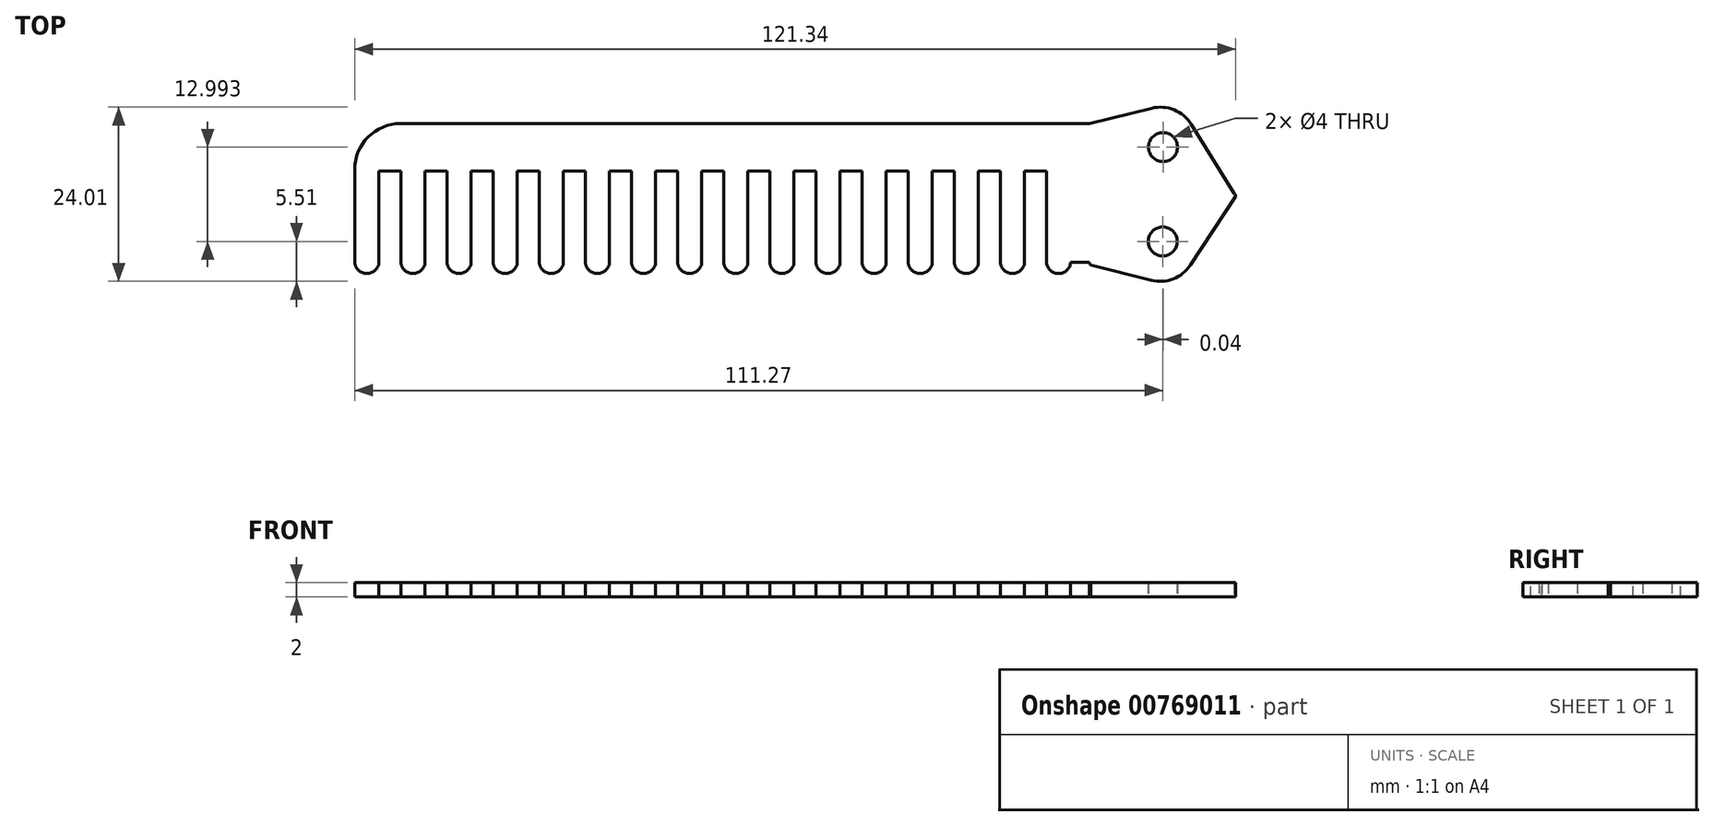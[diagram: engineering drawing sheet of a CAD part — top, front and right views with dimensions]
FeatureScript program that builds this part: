
annotation { "Feature Type Name" : "Feature", "Feature Type Description" : "" }
export const myFeature = defineFeature(function(context is Context, id is Id, definition is map)
    precondition{}
    {
        {
            var Q0;
            Q0=qCreatedBy(makeId("Top.planeOp"),FACE);
            var sketch = newSketch(context, id + "F0", { "sketchPlane" : qUnion([Q0])});
            skLineSegment(sketch, "E0", {"start": v(-47.53, 12.92) * mm, "end": v(-47.53, 1.96) * mm});
            skArc(sketch, "E1.filletArc", {"start": v(-44.5, 15.95) * mm, "mid": v(-46.64, 15.07) * mm, "end": v(-47.53, 12.92) * mm});
            skArc(sketch, "E2.filletArc", {"start": v(58.65, -3.18) * mm, "mid": v(58.7, -3.38) * mm, "end": v(58.81, -3.55) * mm});
            skLineSegment(sketch, "E3", {"start": v(78.8, 5.95) * mm, "end": v(78.8, 5.95) * mm});
            skLineSegment(sketch, "E4", {"start": v(-44.5, 15.95) * mm, "end": v(58.65, 15.95) * mm});
            skPoint(sketch, "E5.visualSharp", {"position": v(78.8, -4.05) * mm});
            skPoint(sketch, "E6.visualSharp", {"position": v(78.8, 15.95) * mm});
            skPoint(sketch, "E7.visualSharp", {"position": v(78.8, 5.95) * mm});
            skCircle(sketch, "E8", {"center": v(68.73, -0.29) * mm, "radius": 2 * mm});
            skCircle(sketch, "E9", {"center": v(68.77, 12.7) * mm, "radius": 2 * mm});
            skLineSegment(sketch, "E10", {"start": v(72.54, -3.55) * mm, "end": v(78.8, 5.94) * mm});
            skLineSegment(sketch, "E11", {"start": v(72.66, 15.85) * mm, "end": v(78.6, 6.3) * mm});
            skLineSegment(sketch, "E12", {"start": v(58.65, 15.95) * mm, "end": v(67.22, 18.06) * mm});
            skLineSegment(sketch, "E13", {"start": v(58.81, -3.55) * mm, "end": v(67.14, -5.65) * mm});
            skPoint(sketch, "E14.visualSharp", {"position": v(70.75, 18.93) * mm});
            skArc(sketch, "E14.filletArc", {"start": v(72.66, 15.85) * mm, "mid": v(70.3, 17.84) * mm, "end": v(67.22, 18.06) * mm});
            skPoint(sketch, "E15.visualSharp", {"position": v(70.58, -6.52) * mm});
            skArc(sketch, "E15.filletArc", {"start": v(67.14, -5.65) * mm, "mid": v(70.17, -5.46) * mm, "end": v(72.54, -3.55) * mm});
            skArc(sketch, "E16", {"start": v(78.8, 5.94) * mm, "mid": v(78.72, 6.13) * mm, "end": v(78.6, 6.3) * mm});
            skLineSegment(sketch, "E17", {"start": v(-42.54, -3.04) * mm, "end": v(58.65, -3.18) * mm});
            skPoint(sketch, "E18.visualSharp", {"position": v(-47.53, -3.03) * mm});
            skArc(sketch, "E18.filletArc", {"start": v(-47.53, 1.96) * mm, "mid": v(-46.07, -1.57) * mm, "end": v(-42.54, -3.04) * mm});
            skSolve(sketch);
        }
        {
            var Q0;
            Q0=qSketchRegion(id+"F0",true);
            var Q1;
            Q1=makeQuery(id+"F0.imprint","IMPRINT",FACE,{"disambiguationData":[TD([[makeQuery(id+"F0.imprint","IMPRINT",EDGE,{"derivedFrom":sQuery(id+"F0.wireOp",EDGE,"1oXmgVZ5-gnLq-iHea-oESG-ihjMs6EF8sqd")}),1.0]])]});
            var Q2;
            Q2=makeQuery(id+"F0.imprint","IMPRINT",FACE,{"disambiguationData":[TD([[makeQuery(id+"F0.imprint","IMPRINT",EDGE,{"derivedFrom":sQuery(id+"F0.wireOp",EDGE,"hkDLLBfR-qxi3-HcG5-FM2N-qt6i9bJRYM3o")}),1.0]])]});
            extrude(context, id + "F1", {"entities" : qUnion([Q0, Q1, Q2]), "depth" : 2 * mm, "offsetDistance" : 25 * mm});
        }
        {
            var Q0;
            Q0=makeQuery(id+"F1.opExtrude","CAP_FACE",FACE,{"disambiguationData":[OSD([sQuery(id+"F0.wireOp",EDGE,"E0"),sQuery(id+"F0.wireOp",EDGE,"E1.filletArc"),sQuery(id+"F0.wireOp",EDGE,"E2.filletArc"),sQuery(id+"F0.wireOp",EDGE,"E4"),sQuery(id+"F0.wireOp",EDGE,"E8"),sQuery(id+"F0.wireOp",EDGE,"E9"),sQuery(id+"F0.wireOp",EDGE,"E10"),sQuery(id+"F0.wireOp",EDGE,"E11"),sQuery(id+"F0.wireOp",EDGE,"E12"),sQuery(id+"F0.wireOp",EDGE,"E13"),sQuery(id+"F0.wireOp",EDGE,"E14.filletArc"),sQuery(id+"F0.wireOp",EDGE,"E15.filletArc"),sQuery(id+"F0.wireOp",EDGE,"E16"),sQuery(id+"F0.wireOp",EDGE,"E17"),sQuery(id+"F0.wireOp",EDGE,"E18.filletArc")])],"isStart":false});
            var sketch = newSketch(context, id + "F2", { "sketchPlane" : qUnion([Q0])});
            skLineSegment(sketch, "E19.0", {"start": v(-36.19, 15.95) * mm, "end": v(58.65, 15.95) * mm});
            skLineSegment(sketch, "E20", {"start": v(-42.54, -3.04) * mm, "end": v(-42.54, 9.41) * mm});
            skLineSegment(sketch, "E21", {"start": v(-42.54, 9.41) * mm, "end": v(-39.18, 9.41) * mm});
            skLineSegment(sketch, "E22", {"start": v(-39.18, 9.41) * mm, "end": v(-39.18, -3.05) * mm});
            skArc(sketch, "E23", {"start": v(-42.54, -3.04) * mm, "mid": v(-40.86, -4.72) * mm, "end": v(-39.18, -3.05) * mm});
            skArc(sketch, "E24.1.0.0", {"start": v(-36.19, -3.04) * mm, "mid": v(-34.51, -4.72) * mm, "end": v(-32.83, -3.05) * mm});
            skLineSegment(sketch, "E24.1.0.1", {"start": v(-32.83, 9.41) * mm, "end": v(-32.83, -3.05) * mm});
            skLineSegment(sketch, "E24.1.0.2", {"start": v(-36.19, 9.41) * mm, "end": v(-32.83, 9.41) * mm});
            skLineSegment(sketch, "E24.1.0.3", {"start": v(-36.19, -3.04) * mm, "end": v(-36.19, 9.41) * mm});
            skArc(sketch, "E24.2.0.0", {"start": v(-29.84, -3.04) * mm, "mid": v(-28.16, -4.72) * mm, "end": v(-26.48, -3.05) * mm});
            skLineSegment(sketch, "E24.2.0.1", {"start": v(-26.48, 9.41) * mm, "end": v(-26.48, -3.05) * mm});
            skLineSegment(sketch, "E24.2.0.2", {"start": v(-29.84, 9.41) * mm, "end": v(-26.48, 9.41) * mm});
            skLineSegment(sketch, "E24.2.0.3", {"start": v(-29.84, -3.04) * mm, "end": v(-29.84, 9.41) * mm});
            skArc(sketch, "E24.3.0.0", {"start": v(-23.49, -3.04) * mm, "mid": v(-21.81, -4.72) * mm, "end": v(-20.13, -3.05) * mm});
            skLineSegment(sketch, "E24.3.0.1", {"start": v(-20.13, 9.41) * mm, "end": v(-20.13, -3.05) * mm});
            skLineSegment(sketch, "E24.3.0.2", {"start": v(-23.49, 9.41) * mm, "end": v(-20.13, 9.41) * mm});
            skLineSegment(sketch, "E24.3.0.3", {"start": v(-23.49, -3.04) * mm, "end": v(-23.49, 9.41) * mm});
            skArc(sketch, "E24.4.0.0", {"start": v(-17.14, -3.04) * mm, "mid": v(-15.46, -4.72) * mm, "end": v(-13.78, -3.05) * mm});
            skLineSegment(sketch, "E24.4.0.1", {"start": v(-13.78, 9.41) * mm, "end": v(-13.78, -3.05) * mm});
            skLineSegment(sketch, "E24.4.0.2", {"start": v(-17.14, 9.41) * mm, "end": v(-13.78, 9.41) * mm});
            skLineSegment(sketch, "E24.4.0.3", {"start": v(-17.14, -3.04) * mm, "end": v(-17.14, 9.41) * mm});
            skArc(sketch, "E24.5.0.0", {"start": v(-10.79, -3.04) * mm, "mid": v(-9.11, -4.72) * mm, "end": v(-7.43, -3.05) * mm});
            skLineSegment(sketch, "E24.5.0.1", {"start": v(-7.43, 9.41) * mm, "end": v(-7.43, -3.05) * mm});
            skLineSegment(sketch, "E24.5.0.2", {"start": v(-10.79, 9.41) * mm, "end": v(-7.43, 9.41) * mm});
            skLineSegment(sketch, "E24.5.0.3", {"start": v(-10.79, -3.04) * mm, "end": v(-10.79, 9.41) * mm});
            skArc(sketch, "E24.6.0.0", {"start": v(-4.44, -3.04) * mm, "mid": v(-2.76, -4.72) * mm, "end": v(-1.08, -3.05) * mm});
            skLineSegment(sketch, "E24.6.0.1", {"start": v(-1.08, 9.41) * mm, "end": v(-1.08, -3.05) * mm});
            skLineSegment(sketch, "E24.6.0.2", {"start": v(-4.44, 9.41) * mm, "end": v(-1.08, 9.41) * mm});
            skLineSegment(sketch, "E24.6.0.3", {"start": v(-4.44, -3.04) * mm, "end": v(-4.44, 9.41) * mm});
            skArc(sketch, "E24.7.0.0", {"start": v(1.91, -3.04) * mm, "mid": v(3.59, -4.72) * mm, "end": v(5.27, -3.05) * mm});
            skLineSegment(sketch, "E24.7.0.1", {"start": v(5.27, 9.41) * mm, "end": v(5.27, -3.05) * mm});
            skLineSegment(sketch, "E24.7.0.2", {"start": v(1.91, 9.41) * mm, "end": v(5.27, 9.41) * mm});
            skLineSegment(sketch, "E24.7.0.3", {"start": v(1.91, -3.04) * mm, "end": v(1.91, 9.41) * mm});
            skArc(sketch, "E24.8.0.0", {"start": v(8.26, -3.04) * mm, "mid": v(9.94, -4.72) * mm, "end": v(11.62, -3.05) * mm});
            skLineSegment(sketch, "E24.8.0.1", {"start": v(11.62, 9.41) * mm, "end": v(11.62, -3.05) * mm});
            skLineSegment(sketch, "E24.8.0.2", {"start": v(8.26, 9.41) * mm, "end": v(11.62, 9.41) * mm});
            skLineSegment(sketch, "E24.8.0.3", {"start": v(8.26, -3.04) * mm, "end": v(8.26, 9.41) * mm});
            skLineSegment(sketch, "E25.1.0.0", {"start": v(17.97, 9.41) * mm, "end": v(17.97, -3.05) * mm});
            skLineSegment(sketch, "E25.1.0.1", {"start": v(14.61, -3.04) * mm, "end": v(14.61, 9.41) * mm});
            skArc(sketch, "E25.1.0.2", {"start": v(14.61, -3.04) * mm, "mid": v(16.29, -4.72) * mm, "end": v(17.97, -3.05) * mm});
            skLineSegment(sketch, "E25.1.0.3", {"start": v(14.61, 9.41) * mm, "end": v(17.97, 9.41) * mm});
            skLineSegment(sketch, "E25.2.0.0", {"start": v(24.32, 9.41) * mm, "end": v(24.32, -3.05) * mm});
            skLineSegment(sketch, "E25.2.0.1", {"start": v(20.96, -3.04) * mm, "end": v(20.96, 9.41) * mm});
            skArc(sketch, "E25.2.0.2", {"start": v(20.96, -3.04) * mm, "mid": v(22.64, -4.72) * mm, "end": v(24.32, -3.05) * mm});
            skLineSegment(sketch, "E25.2.0.3", {"start": v(20.96, 9.41) * mm, "end": v(24.32, 9.41) * mm});
            skLineSegment(sketch, "E25.3.0.0", {"start": v(30.67, 9.41) * mm, "end": v(30.67, -3.05) * mm});
            skLineSegment(sketch, "E25.3.0.1", {"start": v(27.31, -3.04) * mm, "end": v(27.31, 9.41) * mm});
            skArc(sketch, "E25.3.0.2", {"start": v(27.31, -3.04) * mm, "mid": v(28.99, -4.72) * mm, "end": v(30.67, -3.05) * mm});
            skLineSegment(sketch, "E25.3.0.3", {"start": v(27.31, 9.41) * mm, "end": v(30.67, 9.41) * mm});
            skLineSegment(sketch, "E25.4.0.0", {"start": v(37.02, 9.41) * mm, "end": v(37.02, -3.05) * mm});
            skLineSegment(sketch, "E25.4.0.1", {"start": v(33.66, -3.04) * mm, "end": v(33.66, 9.41) * mm});
            skArc(sketch, "E25.4.0.2", {"start": v(33.66, -3.04) * mm, "mid": v(35.34, -4.72) * mm, "end": v(37.02, -3.05) * mm});
            skLineSegment(sketch, "E25.4.0.3", {"start": v(33.66, 9.41) * mm, "end": v(37.02, 9.41) * mm});
            skLineSegment(sketch, "E25.5.0.0", {"start": v(43.37, 9.41) * mm, "end": v(43.37, -3.05) * mm});
            skLineSegment(sketch, "E25.5.0.1", {"start": v(40.01, -3.04) * mm, "end": v(40.01, 9.41) * mm});
            skArc(sketch, "E25.5.0.2", {"start": v(40.01, -3.04) * mm, "mid": v(41.69, -4.72) * mm, "end": v(43.37, -3.05) * mm});
            skLineSegment(sketch, "E25.5.0.3", {"start": v(40.01, 9.41) * mm, "end": v(43.37, 9.41) * mm});
            skLineSegment(sketch, "E25.6.0.0", {"start": v(49.72, 9.41) * mm, "end": v(49.72, -3.05) * mm});
            skLineSegment(sketch, "E25.6.0.1", {"start": v(46.36, -3.04) * mm, "end": v(46.36, 9.41) * mm});
            skArc(sketch, "E25.6.0.2", {"start": v(46.36, -3.04) * mm, "mid": v(48.04, -4.72) * mm, "end": v(49.72, -3.05) * mm});
            skLineSegment(sketch, "E25.6.0.3", {"start": v(46.36, 9.41) * mm, "end": v(49.72, 9.41) * mm});
            skLineSegment(sketch, "E25.7.0.0", {"start": v(56.07, 9.41) * mm, "end": v(56.07, -3.05) * mm});
            skLineSegment(sketch, "E25.7.0.1", {"start": v(52.71, -3.04) * mm, "end": v(52.71, 9.41) * mm});
            skArc(sketch, "E25.7.0.2", {"start": v(52.71, -3.04) * mm, "mid": v(54.39, -4.72) * mm, "end": v(56.07, -3.05) * mm});
            skLineSegment(sketch, "E25.7.0.3", {"start": v(52.71, 9.41) * mm, "end": v(56.07, 9.41) * mm});
            skLineSegment(sketch, "E25.direction1", {"start": v(8.26, -3.04) * mm, "end": v(14.61, -3.04) * mm, "construction": true});
            skLineSegment(sketch, "E26", {"start": v(-39.18, 9.41) * mm, "end": v(-36.19, 9.41) * mm});
            skLineSegment(sketch, "E27", {"start": v(-32.83, 9.41) * mm, "end": v(-29.84, 9.41) * mm});
            skLineSegment(sketch, "E28", {"start": v(-26.48, 9.41) * mm, "end": v(-23.49, 9.41) * mm});
            skLineSegment(sketch, "E29", {"start": v(-20.13, 9.41) * mm, "end": v(-17.14, 9.41) * mm});
            skLineSegment(sketch, "E30", {"start": v(-13.78, 9.41) * mm, "end": v(-10.79, 9.41) * mm});
            skLineSegment(sketch, "E31", {"start": v(-7.43, 9.41) * mm, "end": v(-4.44, 9.41) * mm});
            skLineSegment(sketch, "E32", {"start": v(-1.08, 9.41) * mm, "end": v(1.91, 9.41) * mm});
            skLineSegment(sketch, "E33", {"start": v(5.27, 9.41) * mm, "end": v(8.26, 9.41) * mm});
            skLineSegment(sketch, "E34", {"start": v(11.62, 9.41) * mm, "end": v(14.61, 9.41) * mm});
            skLineSegment(sketch, "E35", {"start": v(17.97, 9.41) * mm, "end": v(20.96, 9.41) * mm});
            skLineSegment(sketch, "E36", {"start": v(24.32, 9.41) * mm, "end": v(27.31, 9.41) * mm});
            skLineSegment(sketch, "E37", {"start": v(30.67, 9.41) * mm, "end": v(33.66, 9.41) * mm});
            skLineSegment(sketch, "E38", {"start": v(37.02, 9.41) * mm, "end": v(40.01, 9.41) * mm});
            skLineSegment(sketch, "E39", {"start": v(43.37, 9.41) * mm, "end": v(46.36, 9.41) * mm});
            skLineSegment(sketch, "E40", {"start": v(49.72, 9.41) * mm, "end": v(52.71, 9.41) * mm});
            skLineSegment(sketch, "E41.0", {"start": v(-42.54, -3.04) * mm, "end": v(58.65, -3.18) * mm});
            skLineSegment(sketch, "E42", {"start": v(-42.54, 9.41) * mm, "end": v(-42.54, 9.6) * mm});
            skPoint(sketch, "E43.orphan", {"position": v(-44.5, 15.95) * mm});
            skPoint(sketch, "E44.visualSharp", {"position": v(-42.54, 15.95) * mm});
            skArc(sketch, "E44.filletArc", {"start": v(-36.19, 15.95) * mm, "mid": v(-40.68, 14.1) * mm, "end": v(-42.54, 9.6) * mm});
            skSolve(sketch);
        }
        {
            var Q0;
            {var subQ4=sQuery(id+"F2.wireOp",EDGE,"E24.4.0.1");Q0=makeQuery(id+"F2.imprint","IMPRINT",FACE,{"disambiguationData":[TD([[makeQuery(id+"F2.imprint","IMPRINT",EDGE,{"derivedFrom":subQ4}),1.0]])]});}
            var Q1;
            {var subQ4=sQuery(id+"F2.wireOp",EDGE,"E24.5.0.1");Q1=makeQuery(id+"F2.imprint","IMPRINT",FACE,{"disambiguationData":[TD([[makeQuery(id+"F2.imprint","IMPRINT",EDGE,{"derivedFrom":subQ4}),1.0]])]});}
            var Q2;
            {var subQ6=sQuery(id+"F2.wireOp",EDGE,"E24.6.0.1");Q2=makeQuery(id+"F2.imprint","IMPRINT",FACE,{"disambiguationData":[TD([[makeQuery(id+"F2.imprint","IMPRINT",EDGE,{"derivedFrom":subQ6}),1.0]])]});}
            var Q3;
            {var subQ4=sQuery(id+"F2.wireOp",EDGE,"E24.7.0.1");Q3=makeQuery(id+"F2.imprint","IMPRINT",FACE,{"disambiguationData":[TD([[makeQuery(id+"F2.imprint","IMPRINT",EDGE,{"derivedFrom":subQ4}),1.0]])]});}
            var Q4;
            {var subQ4=sQuery(id+"F2.wireOp",EDGE,"E24.8.0.1");Q4=makeQuery(id+"F2.imprint","IMPRINT",FACE,{"disambiguationData":[TD([[makeQuery(id+"F2.imprint","IMPRINT",EDGE,{"derivedFrom":subQ4}),1.0]])]});}
            var Q5;
            {var subQ5=sQuery(id+"F2.wireOp",EDGE,"E25.1.0.0");Q5=makeQuery(id+"F2.imprint","IMPRINT",FACE,{"disambiguationData":[TD([[makeQuery(id+"F2.imprint","IMPRINT",EDGE,{"derivedFrom":subQ5}),1.0]])]});}
            var Q6;
            {var subQ5=sQuery(id+"F2.wireOp",EDGE,"E25.2.0.0");Q6=makeQuery(id+"F2.imprint","IMPRINT",FACE,{"disambiguationData":[TD([[makeQuery(id+"F2.imprint","IMPRINT",EDGE,{"derivedFrom":subQ5}),1.0]])]});}
            var Q7;
            {var subQ5=sQuery(id+"F2.wireOp",EDGE,"E25.3.0.0");Q7=makeQuery(id+"F2.imprint","IMPRINT",FACE,{"disambiguationData":[TD([[makeQuery(id+"F2.imprint","IMPRINT",EDGE,{"derivedFrom":subQ5}),1.0]])]});}
            var Q8;
            {var subQ5=sQuery(id+"F2.wireOp",EDGE,"E25.4.0.0");Q8=makeQuery(id+"F2.imprint","IMPRINT",FACE,{"disambiguationData":[TD([[makeQuery(id+"F2.imprint","IMPRINT",EDGE,{"derivedFrom":subQ5}),1.0]])]});}
            var Q9;
            {var subQ5=sQuery(id+"F2.wireOp",EDGE,"E25.5.0.0");Q9=makeQuery(id+"F2.imprint","IMPRINT",FACE,{"disambiguationData":[TD([[makeQuery(id+"F2.imprint","IMPRINT",EDGE,{"derivedFrom":subQ5}),1.0]])]});}
            var Q10;
            {var subQ5=sQuery(id+"F2.wireOp",EDGE,"E25.6.0.0");Q10=makeQuery(id+"F2.imprint","IMPRINT",FACE,{"disambiguationData":[TD([[makeQuery(id+"F2.imprint","IMPRINT",EDGE,{"derivedFrom":subQ5}),1.0]])]});}
            var Q11;
            {var subQ4=sQuery(id+"F2.wireOp",EDGE,"E24.3.0.1");Q11=makeQuery(id+"F2.imprint","IMPRINT",FACE,{"disambiguationData":[TD([[makeQuery(id+"F2.imprint","IMPRINT",EDGE,{"derivedFrom":subQ4}),1.0]])]});}
            var Q12;
            {var subQ4=sQuery(id+"F2.wireOp",EDGE,"E24.2.0.1");Q12=makeQuery(id+"F2.imprint","IMPRINT",FACE,{"disambiguationData":[TD([[makeQuery(id+"F2.imprint","IMPRINT",EDGE,{"derivedFrom":subQ4}),1.0]])]});}
            var Q13;
            {var subQ4=sQuery(id+"F2.wireOp",EDGE,"E24.1.0.1");Q13=makeQuery(id+"F2.imprint","IMPRINT",FACE,{"disambiguationData":[TD([[makeQuery(id+"F2.imprint","IMPRINT",EDGE,{"derivedFrom":subQ4}),1.0]])]});}
            var Q14;
            {var subQ4=sQuery(id+"F2.wireOp",EDGE,"E22");Q14=makeQuery(id+"F2.imprint","IMPRINT",FACE,{"disambiguationData":[TD([[makeQuery(id+"F2.imprint","IMPRINT",EDGE,{"derivedFrom":subQ4}),1.0]])]});}
            extrude(context, id + "F3", {"entities" : qUnion([Q0, Q1, Q2, Q3, Q4, Q5, Q6, Q7, Q8, Q9, Q10, Q11, Q12, Q13, Q14]), "operationType" : NewBodyOperationType.REMOVE, "oppositeDirection" : true, "depth" : 25.4 * mm, "offsetDistance" : 25.4 * mm});
        }
        {
            var Q0;
            {var subQ0=sQuery(id+"F2.wireOp",EDGE,"E41.0");var subQ1=sQuery(id+"F2.wireOp",EDGE,"E25.7.0.2");var subQ2=makeQuery(id+"F2.imprint","INTERSECT",VERTEX,{"disambiguationData":[OD(0.0)],"derivedFrom":[subQ1,subQ0]});Q0=makeQuery(id+"F2.imprint","IMPRINT",FACE,{"disambiguationData":[TD([[makeQuery(id+"F2.imprint","IMPRINT",EDGE,{"disambiguationData":[TD([[subQ2,-1.0]])],"derivedFrom":subQ1}),1.0]])]});}
            var Q1;
            {var subQ0=sQuery(id+"F2.wireOp",EDGE,"E41.0");var subQ1=sQuery(id+"F2.wireOp",EDGE,"E25.6.0.2");var subQ2=makeQuery(id+"F2.imprint","INTERSECT",VERTEX,{"disambiguationData":[OD(0.0)],"derivedFrom":[subQ1,subQ0]});Q1=makeQuery(id+"F2.imprint","IMPRINT",FACE,{"disambiguationData":[TD([[makeQuery(id+"F2.imprint","IMPRINT",EDGE,{"disambiguationData":[TD([[subQ2,-1.0]])],"derivedFrom":subQ1}),1.0]])]});}
            var Q2;
            {var subQ0=sQuery(id+"F2.wireOp",EDGE,"E41.0");var subQ1=sQuery(id+"F2.wireOp",EDGE,"E25.5.0.2");var subQ2=makeQuery(id+"F2.imprint","INTERSECT",VERTEX,{"disambiguationData":[OD(0.0)],"derivedFrom":[subQ1,subQ0]});Q2=makeQuery(id+"F2.imprint","IMPRINT",FACE,{"disambiguationData":[TD([[makeQuery(id+"F2.imprint","IMPRINT",EDGE,{"disambiguationData":[TD([[subQ2,-1.0]])],"derivedFrom":subQ1}),1.0]])]});}
            var Q3;
            {var subQ0=sQuery(id+"F2.wireOp",EDGE,"E41.0");var subQ1=sQuery(id+"F2.wireOp",EDGE,"E25.4.0.2");var subQ2=makeQuery(id+"F2.imprint","INTERSECT",VERTEX,{"disambiguationData":[OD(0.0)],"derivedFrom":[subQ1,subQ0]});Q3=makeQuery(id+"F2.imprint","IMPRINT",FACE,{"disambiguationData":[TD([[makeQuery(id+"F2.imprint","IMPRINT",EDGE,{"disambiguationData":[TD([[subQ2,-1.0]])],"derivedFrom":subQ1}),1.0]])]});}
            var Q4;
            {var subQ0=sQuery(id+"F2.wireOp",EDGE,"E41.0");var subQ1=sQuery(id+"F2.wireOp",EDGE,"E25.3.0.2");var subQ2=makeQuery(id+"F2.imprint","INTERSECT",VERTEX,{"disambiguationData":[OD(0.0)],"derivedFrom":[subQ1,subQ0]});Q4=makeQuery(id+"F2.imprint","IMPRINT",FACE,{"disambiguationData":[TD([[makeQuery(id+"F2.imprint","IMPRINT",EDGE,{"disambiguationData":[TD([[subQ2,-1.0]])],"derivedFrom":subQ1}),1.0]])]});}
            var Q5;
            {var subQ0=sQuery(id+"F2.wireOp",EDGE,"E41.0");var subQ1=sQuery(id+"F2.wireOp",EDGE,"E25.2.0.2");var subQ2=makeQuery(id+"F2.imprint","INTERSECT",VERTEX,{"disambiguationData":[OD(0.0)],"derivedFrom":[subQ1,subQ0]});Q5=makeQuery(id+"F2.imprint","IMPRINT",FACE,{"disambiguationData":[TD([[makeQuery(id+"F2.imprint","IMPRINT",EDGE,{"disambiguationData":[TD([[subQ2,-1.0]])],"derivedFrom":subQ1}),1.0]])]});}
            var Q6;
            {var subQ0=sQuery(id+"F2.wireOp",EDGE,"E41.0");var subQ1=sQuery(id+"F2.wireOp",EDGE,"E25.1.0.2");var subQ2=makeQuery(id+"F2.imprint","INTERSECT",VERTEX,{"disambiguationData":[OD(0.0)],"derivedFrom":[subQ1,subQ0]});Q6=makeQuery(id+"F2.imprint","IMPRINT",FACE,{"disambiguationData":[TD([[makeQuery(id+"F2.imprint","IMPRINT",EDGE,{"disambiguationData":[TD([[subQ2,-1.0]])],"derivedFrom":subQ1}),1.0]])]});}
            var Q7;
            {var subQ0=sQuery(id+"F2.wireOp",EDGE,"E41.0");var subQ1=sQuery(id+"F2.wireOp",EDGE,"E24.8.0.0");var subQ2=makeQuery(id+"F2.imprint","INTERSECT",VERTEX,{"disambiguationData":[OD(0.0)],"derivedFrom":[subQ1,subQ0]});Q7=makeQuery(id+"F2.imprint","IMPRINT",FACE,{"disambiguationData":[TD([[makeQuery(id+"F2.imprint","IMPRINT",EDGE,{"disambiguationData":[TD([[subQ2,-1.0]])],"derivedFrom":subQ1}),1.0]])]});}
            var Q8;
            {var subQ0=sQuery(id+"F2.wireOp",EDGE,"E41.0");var subQ1=sQuery(id+"F2.wireOp",EDGE,"E24.7.0.0");var subQ2=makeQuery(id+"F2.imprint","INTERSECT",VERTEX,{"disambiguationData":[OD(0.0)],"derivedFrom":[subQ1,subQ0]});Q8=makeQuery(id+"F2.imprint","IMPRINT",FACE,{"disambiguationData":[TD([[makeQuery(id+"F2.imprint","IMPRINT",EDGE,{"disambiguationData":[TD([[subQ2,-1.0]])],"derivedFrom":subQ1}),1.0]])]});}
            var Q9;
            {var subQ0=sQuery(id+"F2.wireOp",EDGE,"E41.0");var subQ1=sQuery(id+"F2.wireOp",EDGE,"E24.6.0.0");var subQ2=makeQuery(id+"F2.imprint","INTERSECT",VERTEX,{"disambiguationData":[OD(0.0)],"derivedFrom":[subQ1,subQ0]});Q9=makeQuery(id+"F2.imprint","IMPRINT",FACE,{"disambiguationData":[TD([[makeQuery(id+"F2.imprint","IMPRINT",EDGE,{"disambiguationData":[TD([[subQ2,-1.0]])],"derivedFrom":subQ1}),1.0]])]});}
            var Q10;
            {var subQ0=sQuery(id+"F2.wireOp",EDGE,"E41.0");var subQ1=sQuery(id+"F2.wireOp",EDGE,"E24.5.0.0");var subQ2=makeQuery(id+"F2.imprint","INTERSECT",VERTEX,{"disambiguationData":[OD(0.0)],"derivedFrom":[subQ1,subQ0]});Q10=makeQuery(id+"F2.imprint","IMPRINT",FACE,{"disambiguationData":[TD([[makeQuery(id+"F2.imprint","IMPRINT",EDGE,{"disambiguationData":[TD([[subQ2,-1.0]])],"derivedFrom":subQ1}),1.0]])]});}
            var Q11;
            {var subQ0=sQuery(id+"F2.wireOp",EDGE,"E41.0");var subQ1=sQuery(id+"F2.wireOp",EDGE,"E24.4.0.0");var subQ2=makeQuery(id+"F2.imprint","INTERSECT",VERTEX,{"disambiguationData":[OD(0.0)],"derivedFrom":[subQ1,subQ0]});Q11=makeQuery(id+"F2.imprint","IMPRINT",FACE,{"disambiguationData":[TD([[makeQuery(id+"F2.imprint","IMPRINT",EDGE,{"disambiguationData":[TD([[subQ2,-1.0]])],"derivedFrom":subQ1}),1.0]])]});}
            var Q12;
            {var subQ0=sQuery(id+"F2.wireOp",EDGE,"E41.0");var subQ1=sQuery(id+"F2.wireOp",EDGE,"E24.3.0.0");var subQ2=makeQuery(id+"F2.imprint","INTERSECT",VERTEX,{"disambiguationData":[OD(0.0)],"derivedFrom":[subQ1,subQ0]});Q12=makeQuery(id+"F2.imprint","IMPRINT",FACE,{"disambiguationData":[TD([[makeQuery(id+"F2.imprint","IMPRINT",EDGE,{"disambiguationData":[TD([[subQ2,-1.0]])],"derivedFrom":subQ1}),1.0]])]});}
            var Q13;
            {var subQ0=sQuery(id+"F2.wireOp",EDGE,"E41.0");var subQ1=sQuery(id+"F2.wireOp",EDGE,"E24.2.0.0");var subQ2=makeQuery(id+"F2.imprint","INTERSECT",VERTEX,{"disambiguationData":[OD(0.0)],"derivedFrom":[subQ1,subQ0]});Q13=makeQuery(id+"F2.imprint","IMPRINT",FACE,{"disambiguationData":[TD([[makeQuery(id+"F2.imprint","IMPRINT",EDGE,{"disambiguationData":[TD([[subQ2,-1.0]])],"derivedFrom":subQ1}),1.0]])]});}
            var Q14;
            {var subQ0=sQuery(id+"F2.wireOp",EDGE,"E41.0");var subQ1=sQuery(id+"F2.wireOp",EDGE,"E24.1.0.0");var subQ2=makeQuery(id+"F2.imprint","INTERSECT",VERTEX,{"disambiguationData":[OD(0.0)],"derivedFrom":[subQ1,subQ0]});Q14=makeQuery(id+"F2.imprint","IMPRINT",FACE,{"disambiguationData":[TD([[makeQuery(id+"F2.imprint","IMPRINT",EDGE,{"disambiguationData":[TD([[subQ2,-1.0]])],"derivedFrom":subQ1}),1.0]])]});}
            var Q15;
            {var subQ0=sQuery(id+"F2.wireOp",EDGE,"E23");Q15=makeQuery(id+"F2.imprint","IMPRINT",FACE,{"disambiguationData":[TD([[makeQuery(id+"F2.imprint","IMPRINT",EDGE,{"derivedFrom":subQ0}),1.0]])]});}
            extrude(context, id + "F4", {"entities" : qUnion([Q0, Q1, Q2, Q3, Q4, Q5, Q6, Q7, Q8, Q9, Q10, Q11, Q12, Q13, Q14, Q15]), "operationType" : NewBodyOperationType.ADD, "oppositeDirection" : true, "depth" : 2 * mm, "offsetDistance" : 25.4 * mm});
        }
        {
            var Q0;
            Q0=makeQuery(id+"F2.imprint","IMPRINT",FACE,{"disambiguationData":[TD([[makeQuery(id+"F2.imprint","IMPRINT",EDGE,{"derivedFrom":sQuery(id+"F2.wireOp",EDGE,"E20")}),1.0]])]});
            extrude(context, id + "F5", {"entities" : qUnion([Q0]), "operationType" : NewBodyOperationType.REMOVE, "oppositeDirection" : true, "depth" : 25.4 * mm, "offsetDistance" : 25.4 * mm});
        }
    });
